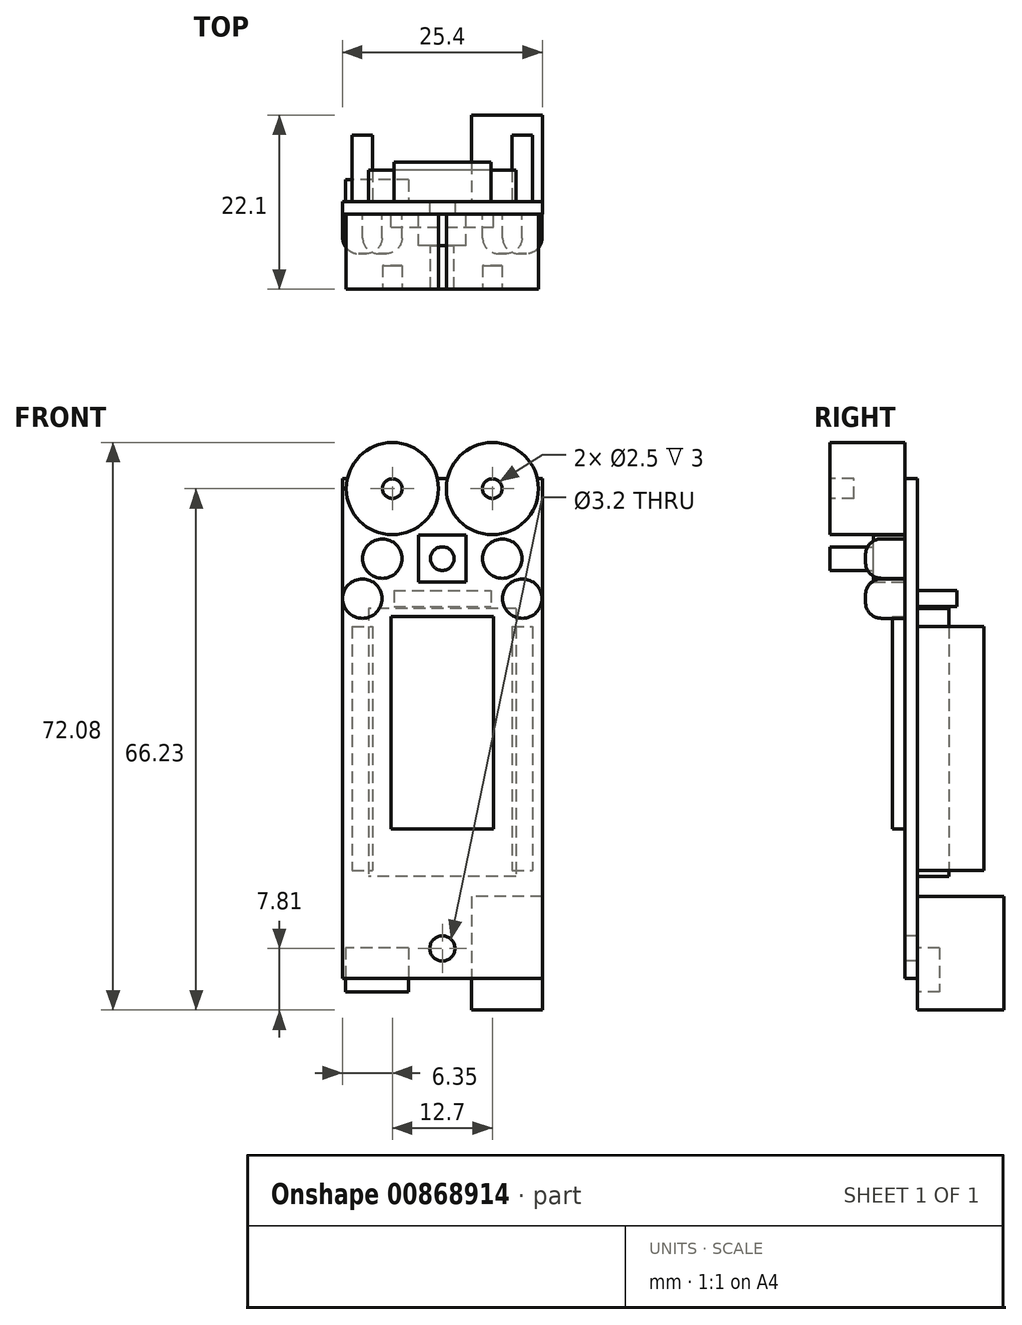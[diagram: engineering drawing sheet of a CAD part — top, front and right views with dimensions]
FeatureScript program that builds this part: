
annotation { "Feature Type Name" : "Feature", "Feature Type Description" : "" }
export const myFeature = defineFeature(function(context is Context, id is Id, definition is map)
    precondition{}
    {
        {
            var Q0;
            Q0=qCreatedBy(makeId("Front.planeOp"),FACE);
            var sketch = newSketch(context, id + "F0", { "sketchPlane" : qUnion([Q0])});
            skLineSegment(sketch, "E0.bottom", {"start": v(-12.7, 10.16) * mm, "end": v(12.7, 10.16) * mm});
            skLineSegment(sketch, "E0.top", {"start": v(-12.7, -53.34) * mm, "end": v(12.7, -53.34) * mm});
            skLineSegment(sketch, "E0.left", {"start": v(-12.7, 10.16) * mm, "end": v(-12.7, -53.34) * mm});
            skLineSegment(sketch, "E0.right", {"start": v(12.7, 10.16) * mm, "end": v(12.7, -53.34) * mm});
            skCircle(sketch, "E1", {"center": v(0, -49.53) * mm, "radius": 1.6 * mm});
            skSolve(sketch);
        }
        {
            var Q0;
            Q0 = qSketchRegion(id + "F0", true);
            extrude(context, id + "F1", {"entities" : qUnion([Q0]), "oppositeDirection" : true, "depth" : 1.6 * mm, "offsetDistance" : 25.4 * mm});
        }
        {
            var Q0;
            Q0=qCreatedBy(makeId("Front.planeOp"),FACE);
            var sketch = newSketch(context, id + "F2", { "sketchPlane" : qUnion([Q0])});
            skLineSegment(sketch, "E2.bottom", {"start": v(3, -3) * mm, "end": v(-3, -3) * mm});
            skLineSegment(sketch, "E2.top", {"start": v(3, 3) * mm, "end": v(-3, 3) * mm});
            skLineSegment(sketch, "E2.left", {"start": v(3, -3) * mm, "end": v(3, 3) * mm});
            skLineSegment(sketch, "E2.right", {"start": v(-3, -3) * mm, "end": v(-3, 3) * mm});
            skPoint(sketch, "E2.middle", {"position": v(0, 0) * mm});
            skSolve(sketch);
        }
        {
            var Q0;
            Q0 = qSketchRegion(id + "F2", true);
            extrude(context, id + "F3", {"entities" : qUnion([Q0]), "depth" : 4 * mm, "offsetDistance" : 25.4 * mm});
        }
        {
            var Q0;
            Q0=qCreatedBy(makeId("Front.planeOp"),FACE);
            var sketch = newSketch(context, id + "F4", { "sketchPlane" : qUnion([Q0])});
            skCircle(sketch, "E3", {"center": v(0, 0) * mm, "radius": 1.5 * mm});
            skSolve(sketch);
        }
        {
            var Q0;
            Q0 = qSketchRegion(id + "F4", true);
            extrude(context, id + "F5", {"entities" : qUnion([Q0]), "operationType" : NewBodyOperationType.ADD, "depth" : 9.5 * mm, "offsetDistance" : 25.4 * mm});
        }
        {
            var Q0;
            Q0=qCreatedBy(makeId("Front.planeOp"),FACE);
            var sketch = newSketch(context, id + "F6", { "sketchPlane" : qUnion([Q0])});
            skCircle(sketch, "E4", {"center": v(-6.35, 8.89) * mm, "radius": 5.85 * mm});
            skCircle(sketch, "E5", {"center": v(6.35, 8.9) * mm, "radius": 5.85 * mm});
            skLineSegment(sketch, "E6", {"start": v(0, 15.49) * mm, "end": v(0, -15.49) * mm, "construction": true});
            skSolve(sketch);
        }
        {
            var Q0;
            Q0 = qSketchRegion(id + "F6", true);
            extrude(context, id + "F7", {"entities" : qUnion([Q0]), "depth" : 9.5 * mm, "offsetDistance" : 25.4 * mm});
        }
        {
            var Q0;
            Q0=qCreatedBy(makeId("Front.planeOp"),FACE);
            var sketch = newSketch(context, id + "F8", { "sketchPlane" : qUnion([Q0])});
            skLineSegment(sketch, "E7.bottom", {"start": v(-6.5, -7.37) * mm, "end": v(6.5, -7.37) * mm});
            skLineSegment(sketch, "E7.top", {"start": v(-6.5, -34.37) * mm, "end": v(6.5, -34.37) * mm});
            skLineSegment(sketch, "E7.left", {"start": v(-6.5, -7.37) * mm, "end": v(-6.5, -34.37) * mm});
            skLineSegment(sketch, "E7.right", {"start": v(6.5, -7.37) * mm, "end": v(6.5, -34.37) * mm});
            skSolve(sketch);
        }
        {
            var Q0;
            Q0 = qSketchRegion(id + "F8", true);
            extrude(context, id + "F9", {"entities" : qUnion([Q0]), "depth" : 1.6 * mm, "offsetDistance" : 25.4 * mm});
        }
        {
            var Q0;
            Q0=makeQuery(id+"F1.opExtrude","CAP_FACE",FACE,{"disambiguationData":[OSD([sQuery(id+"F0.wireOp",EDGE,"E0.bottom"),sQuery(id+"F0.wireOp",EDGE,"E0.top"),sQuery(id+"F0.wireOp",EDGE,"E0.left"),sQuery(id+"F0.wireOp",EDGE,"E0.right"),sQuery(id+"F0.wireOp",EDGE,"E1")])],"isStart":false});
            var sketch = newSketch(context, id + "F10", { "sketchPlane" : qUnion([Q0])});
            skLineSegment(sketch, "E8.bottom", {"start": v(-9.35, -6.35) * mm, "end": v(9.35, -6.35) * mm});
            skLineSegment(sketch, "E8.top", {"start": v(-9.35, -40.35) * mm, "end": v(9.35, -40.35) * mm});
            skLineSegment(sketch, "E8.left", {"start": v(-9.35, -6.35) * mm, "end": v(-9.35, -40.35) * mm});
            skLineSegment(sketch, "E8.right", {"start": v(9.35, -6.35) * mm, "end": v(9.35, -40.35) * mm});
            skSolve(sketch);
        }
        {
            var Q0;
            Q0 = qSketchRegion(id + "F10", true);
            extrude(context, id + "F11", {"entities" : qUnion([Q0]), "depth" : 4 * mm, "offsetDistance" : 25.4 * mm});
        }
        {
            var Q0;
            Q0=makeQuery(id+"F1.opExtrude","CAP_FACE",FACE,{"disambiguationData":[OSD([sQuery(id+"F0.wireOp",EDGE,"E0.bottom"),sQuery(id+"F0.wireOp",EDGE,"E0.top"),sQuery(id+"F0.wireOp",EDGE,"E0.left"),sQuery(id+"F0.wireOp",EDGE,"E0.right"),sQuery(id+"F0.wireOp",EDGE,"E1")])],"isStart":false});
            var sketch = newSketch(context, id + "F12", { "sketchPlane" : qUnion([Q0])});
            skLineSegment(sketch, "E9.top", {"start": v(8.86, -39.64) * mm, "end": v(11.46, -39.64) * mm});
            skLineSegment(sketch, "E10.bottom", {"start": v(-8.86, -8.63) * mm, "end": v(-11.46, -8.63) * mm});
            skLineSegment(sketch, "E10.top", {"start": v(-8.86, -39.63) * mm, "end": v(-11.46, -39.63) * mm});
            skLineSegment(sketch, "E10.left", {"start": v(-8.86, -8.63) * mm, "end": v(-8.86, -39.63) * mm});
            skLineSegment(sketch, "E10.right", {"start": v(-11.46, -8.63) * mm, "end": v(-11.46, -39.63) * mm});
            skPoint(sketch, "E10.middle", {"position": v(-10.16, -24.13) * mm});
            skLineSegment(sketch, "E11.bottom", {"start": v(11.46, -8.63) * mm, "end": v(8.86, -8.63) * mm});
            skLineSegment(sketch, "E11.top", {"start": v(11.46, -39.63) * mm, "end": v(8.86, -39.63) * mm});
            skLineSegment(sketch, "E11.left", {"start": v(11.46, -8.63) * mm, "end": v(11.46, -39.63) * mm});
            skLineSegment(sketch, "E11.right", {"start": v(8.86, -8.63) * mm, "end": v(8.86, -39.63) * mm});
            skPoint(sketch, "E11.middle", {"position": v(10.16, -24.13) * mm});
            skSolve(sketch);
        }
        {
            var Q0;
            Q0 = qSketchRegion(id + "F12", true);
            extrude(context, id + "F13", {"entities" : qUnion([Q0]), "depth" : 8.45 * mm, "offsetDistance" : 25.4 * mm});
        }
        {
            var Q0;
            Q0=makeQuery(id+"F1.opExtrude","CAP_FACE",FACE,{"disambiguationData":[OSD([sQuery(id+"F0.wireOp",EDGE,"E0.bottom"),sQuery(id+"F0.wireOp",EDGE,"E0.top"),sQuery(id+"F0.wireOp",EDGE,"E0.left"),sQuery(id+"F0.wireOp",EDGE,"E0.right"),sQuery(id+"F0.wireOp",EDGE,"E1")])],"isStart":false});
            var sketch = newSketch(context, id + "F14", { "sketchPlane" : qUnion([Q0])});
            skLineSegment(sketch, "E12.bottom", {"start": v(-12.7, -42.94) * mm, "end": v(-3.7, -42.94) * mm});
            skLineSegment(sketch, "E12.top", {"start": v(-12.7, -57.34) * mm, "end": v(-3.7, -57.34) * mm});
            skLineSegment(sketch, "E12.left", {"start": v(-12.7, -42.94) * mm, "end": v(-12.7, -57.34) * mm});
            skLineSegment(sketch, "E12.right", {"start": v(-3.7, -42.94) * mm, "end": v(-3.7, -57.34) * mm});
            skSolve(sketch);
        }
        {
            var Q0;
            Q0 = qSketchRegion(id + "F14", true);
            extrude(context, id + "F15", {"entities" : qUnion([Q0]), "depth" : 11 * mm, "offsetDistance" : 25.4 * mm});
        }
        {
            var Q0;
            Q0=makeQuery(id+"F1.opExtrude","CAP_FACE",FACE,{"disambiguationData":[OSD([sQuery(id+"F0.wireOp",EDGE,"E0.bottom"),sQuery(id+"F0.wireOp",EDGE,"E0.top"),sQuery(id+"F0.wireOp",EDGE,"E0.left"),sQuery(id+"F0.wireOp",EDGE,"E0.right"),sQuery(id+"F0.wireOp",EDGE,"E1")])],"isStart":false});
            var sketch = newSketch(context, id + "F16", { "sketchPlane" : qUnion([Q0])});
            skLineSegment(sketch, "E13.bottom", {"start": v(4.3, -49.44) * mm, "end": v(12.3, -49.44) * mm});
            skLineSegment(sketch, "E13.top", {"start": v(4.3, -55.04) * mm, "end": v(12.3, -55.04) * mm});
            skLineSegment(sketch, "E13.left", {"start": v(4.3, -49.44) * mm, "end": v(4.3, -55.04) * mm});
            skLineSegment(sketch, "E13.right", {"start": v(12.3, -49.44) * mm, "end": v(12.3, -55.04) * mm});
            skSolve(sketch);
        }
        {
            var Q0;
            Q0 = qSketchRegion(id + "F16", true);
            extrude(context, id + "F17", {"entities" : qUnion([Q0]), "depth" : 2.8 * mm, "offsetDistance" : 25.4 * mm});
        }
        {
            var Q0;
            Q0=makeQuery(id+"F1.opExtrude","CAP_FACE",FACE,{"disambiguationData":[OSD([sQuery(id+"F0.wireOp",EDGE,"E0.bottom"),sQuery(id+"F0.wireOp",EDGE,"E0.top"),sQuery(id+"F0.wireOp",EDGE,"E0.left"),sQuery(id+"F0.wireOp",EDGE,"E0.right"),sQuery(id+"F0.wireOp",EDGE,"E1")])],"isStart":false});
            var sketch = newSketch(context, id + "F18", { "sketchPlane" : qUnion([Q0])});
            skLineSegment(sketch, "E14.bottom", {"start": v(6.15, -4.08) * mm, "end": v(-6.15, -4.08) * mm});
            skLineSegment(sketch, "E14.top", {"start": v(6.15, -6.08) * mm, "end": v(-6.15, -6.08) * mm});
            skLineSegment(sketch, "E14.left", {"start": v(6.15, -4.08) * mm, "end": v(6.15, -6.08) * mm});
            skLineSegment(sketch, "E14.right", {"start": v(-6.15, -4.08) * mm, "end": v(-6.15, -6.08) * mm});
            skPoint(sketch, "E14.middle", {"position": v(0, -5.08) * mm});
            skSolve(sketch);
        }
        {
            var Q0;
            Q0 = qSketchRegion(id + "F18", true);
            extrude(context, id + "F19", {"entities" : qUnion([Q0]), "depth" : 5 * mm, "offsetDistance" : 25.4 * mm});
        }
        {
            var Q0;
            Q0=qCreatedBy(makeId("Front.planeOp"),FACE);
            var sketch = newSketch(context, id + "F20", { "sketchPlane" : qUnion([Q0])});
            skCircle(sketch, "E15", {"center": v(-7.62, 0) * mm, "radius": 2.5 * mm});
            skCircle(sketch, "E16", {"center": v(7.62, 0) * mm, "radius": 2.5 * mm});
            skCircle(sketch, "E17", {"center": v(10.16, -5.08) * mm, "radius": 2.5 * mm});
            skCircle(sketch, "E18", {"center": v(-10.16, -5.08) * mm, "radius": 2.5 * mm});
            skSolve(sketch);
        }
        {
            var Q0;
            Q0 = qSketchRegion(id + "F20", true);
            extrude(context, id + "F21", {"entities" : qUnion([Q0]), "depth" : 5 * mm, "offsetDistance" : 25.4 * mm});
        }
        {
            var Q0;
            Q0=makeQuery(id+"F21.opExtrude","CAP_FACE",FACE,{"disambiguationData":[OSD([sQuery(id+"F20.wireOp",EDGE,"E18")])],"isStart":false});
            var Q1;
            Q1=makeQuery(id+"F21.opExtrude","CAP_FACE",FACE,{"disambiguationData":[OSD([sQuery(id+"F20.wireOp",EDGE,"E15")])],"isStart":false});
            var Q2;
            Q2=makeQuery(id+"F21.opExtrude","CAP_FACE",FACE,{"disambiguationData":[OSD([sQuery(id+"F20.wireOp",EDGE,"E16")])],"isStart":false});
            var Q3;
            Q3=makeQuery(id+"F21.opExtrude","CAP_FACE",FACE,{"disambiguationData":[OSD([sQuery(id+"F20.wireOp",EDGE,"E17")])],"isStart":false});
            fillet(context, id + "F22", {"entities" : qUnion([Q0, Q1, Q2, Q3]), "radius" : 2 * mm, "tangentPropagation" : true, "allowEdgeOverflow" : false});
        }
        {
            var Q0;
            Q0=makeQuery(id+"F7.opExtrude","CAP_FACE",FACE,{"disambiguationData":[OSD([sQuery(id+"F6.wireOp",EDGE,"E4")])],"isStart":false});
            var sketch = newSketch(context, id + "F23", { "sketchPlane" : qUnion([Q0])});
            skCircle(sketch, "E19", {"center": v(-6.35, 8.89) * mm, "radius": 1.25 * mm});
            skCircle(sketch, "E20", {"center": v(6.35, 8.9) * mm, "radius": 1.25 * mm});
            skSolve(sketch);
        }
        {
            var Q0;
            Q0 = qSketchRegion(id + "F23", true);
            extrude(context, id + "F24", {"entities" : qUnion([Q0]), "operationType" : NewBodyOperationType.REMOVE, "oppositeDirection" : true, "depth" : 3 * mm, "offsetDistance" : 25.4 * mm});
        }
    });
